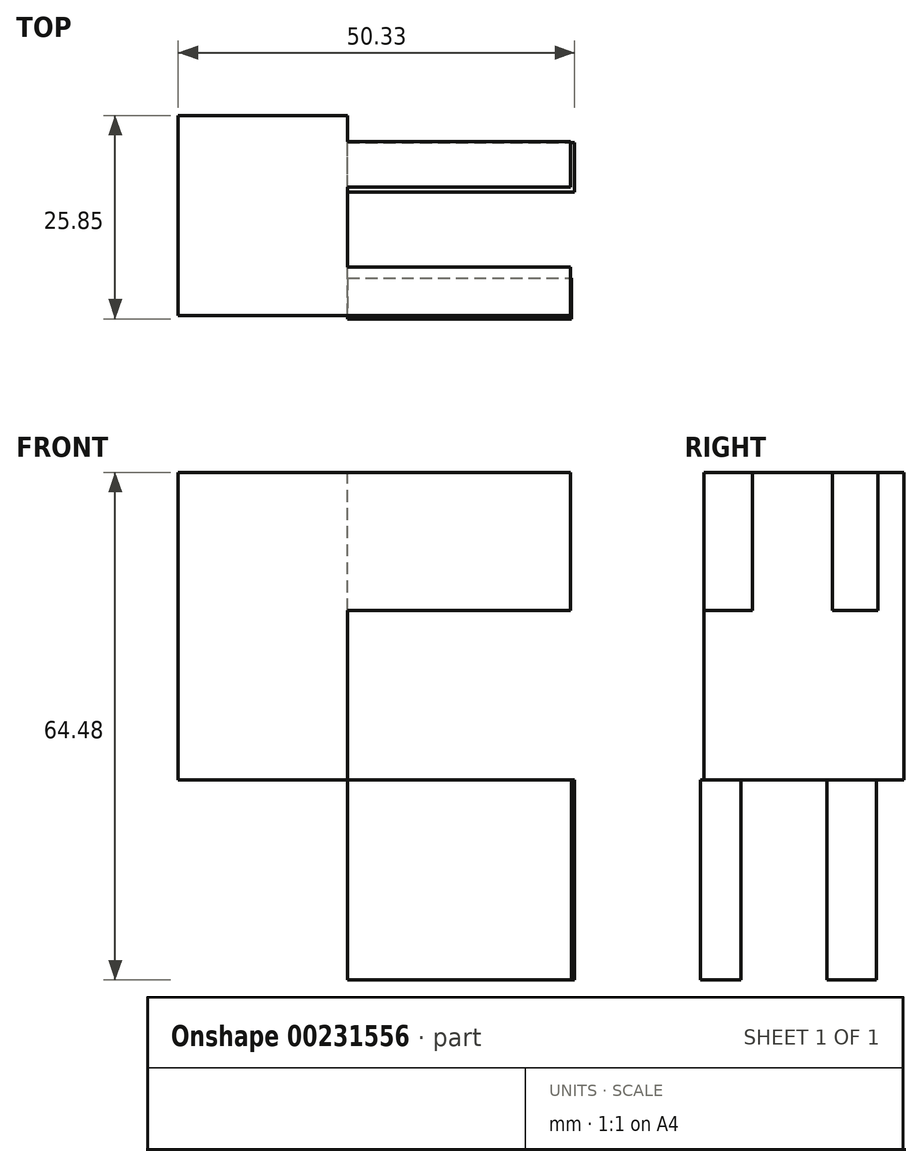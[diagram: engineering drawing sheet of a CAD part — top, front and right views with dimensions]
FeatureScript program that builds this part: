
annotation { "Feature Type Name" : "Feature", "Feature Type Description" : "" }
export const myFeature = defineFeature(function(context is Context, id is Id, definition is map)
    precondition{}
    {
        {
            var Q0;
            Q0=qCreatedBy(makeId("Front.planeOp"),FACE);
            var sketch = newSketch(context, id + "F0", { "sketchPlane" : qUnion([Q0])});
            skLineSegment(sketch, "E0.bottom", {"start": v(-22.74, 6) * mm, "end": v(21.5, 6) * mm});
            skLineSegment(sketch, "E0.top", {"start": v(-22.74, -18.81) * mm, "end": v(21.5, -18.81) * mm});
            skLineSegment(sketch, "E0.left", {"start": v(-22.74, 6) * mm, "end": v(-22.74, -18.81) * mm});
            skLineSegment(sketch, "E0.right", {"start": v(21.5, 6) * mm, "end": v(21.5, -18.81) * mm});
            skSolve(sketch);
        }
        {
            var Q0;
            Q0=makeQuery(id+"F0.imprint","IMPRINT",FACE,{"disambiguationData":[TD([[makeQuery(id+"F0.imprint","IMPRINT",EDGE,{"derivedFrom":sQuery(id+"F0.wireOp",EDGE,"E0.bottom")}),-1.0]])]});
            var sketch = newSketch(context, id + "F1", { "sketchPlane" : qUnion([Q0])});
            skLineSegment(sketch, "E1.bottom", {"start": v(43.2, 14.06) * mm, "end": v(21.7, 14.06) * mm});
            skLineSegment(sketch, "E1.top", {"start": v(43.2, -25.02) * mm, "end": v(21.7, -25.02) * mm});
            skLineSegment(sketch, "E1.left", {"start": v(43.2, 14.06) * mm, "end": v(43.2, -25.02) * mm});
            skLineSegment(sketch, "E1.right", {"start": v(21.7, 14.06) * mm, "end": v(21.7, -25.02) * mm});
            skSolve(sketch);
        }
        {
            var Q0;
            Q0 = qSketchRegion(id + "F1", true);
            extrude(context, id + "F2", {"entities" : qUnion([Q0]), "depth" : 25.4 * mm});
        }
        {
            var Q0;
            Q0=makeQuery(id+"F2.opExtrude","SWEPT_FACE",FACE,{"disambiguationData":[OSD([sQuery(id+"F1.wireOp",EDGE,"E1.bottom")])]});
            var sketch = newSketch(context, id + "F3", { "sketchPlane" : qUnion([Q0])});
            skLineSegment(sketch, "E2.bottom", {"start": v(43.2, -3.3) * mm, "end": v(71.53, -3.3) * mm});
            skLineSegment(sketch, "E2.top", {"start": v(43.2, -9.1) * mm, "end": v(71.53, -9.1) * mm});
            skLineSegment(sketch, "E2.left", {"start": v(43.2, -3.3) * mm, "end": v(43.2, -9.1) * mm});
            skLineSegment(sketch, "E2.right", {"start": v(71.53, -3.3) * mm, "end": v(71.53, -9.1) * mm});
            skLineSegment(sketch, "E3.bottom", {"start": v(43.2, -19.23) * mm, "end": v(71.53, -19.23) * mm});
            skLineSegment(sketch, "E3.top", {"start": v(43.2, -25.4) * mm, "end": v(71.53, -25.4) * mm});
            skLineSegment(sketch, "E3.left", {"start": v(43.2, -19.23) * mm, "end": v(43.2, -25.4) * mm});
            skLineSegment(sketch, "E3.right", {"start": v(71.53, -19.23) * mm, "end": v(71.53, -25.4) * mm});
            skSolve(sketch);
        }
        {
            var Q0;
            Q0=makeQuery(id+"F3.imprint","IMPRINT",FACE,{"disambiguationData":[TD([[makeQuery(id+"F3.imprint","IMPRINT",EDGE,{"derivedFrom":sQuery(id+"F3.wireOp",EDGE,"E3.bottom")}),-1.0]])]});
            var Q1;
            Q1=makeQuery(id+"F3.imprint","IMPRINT",FACE,{"disambiguationData":[TD([[makeQuery(id+"F3.imprint","IMPRINT",EDGE,{"derivedFrom":sQuery(id+"F3.wireOp",EDGE,"E2.bottom")}),-1.0]])]});
            extrude(context, id + "F4", {"entities" : qUnion([Q0, Q1]), "operationType" : NewBodyOperationType.ADD, "oppositeDirection" : true, "depth" : 17.53 * mm});
        }
        {
            var Q0;
            Q0=makeQuery(id+"F2.opExtrude","SWEPT_FACE",FACE,{"disambiguationData":[OSD([sQuery(id+"F1.wireOp",EDGE,"E1.top")])]});
            var sketch = newSketch(context, id + "F5", { "sketchPlane" : qUnion([Q0])});
            skLineSegment(sketch, "E4.left", {"start": v(43.2, 22.95) * mm, "end": v(43.2, 20.67) * mm});
            skLineSegment(sketch, "E4.right", {"start": v(54.17, 22.95) * mm, "end": v(54.17, 20.67) * mm});
            skLineSegment(sketch, "E5.bottom", {"start": v(43.2, 20.67) * mm, "end": v(71.65, 20.67) * mm});
            skLineSegment(sketch, "E5.top", {"start": v(43.2, 25.85) * mm, "end": v(71.65, 25.85) * mm});
            skLineSegment(sketch, "E5.left", {"start": v(43.2, 20.67) * mm, "end": v(43.2, 25.85) * mm});
            skLineSegment(sketch, "E5.right", {"start": v(71.65, 20.67) * mm, "end": v(71.65, 25.85) * mm});
            skLineSegment(sketch, "E6.bottom", {"start": v(43.2, 9.75) * mm, "end": v(72.04, 9.75) * mm});
            skLineSegment(sketch, "E6.top", {"start": v(43.2, 3.47) * mm, "end": v(72.04, 3.47) * mm});
            skLineSegment(sketch, "E6.left", {"start": v(43.2, 9.75) * mm, "end": v(43.2, 3.47) * mm});
            skLineSegment(sketch, "E6.right", {"start": v(72.04, 9.75) * mm, "end": v(72.04, 3.47) * mm});
            skSolve(sketch);
        }
        {
            var Q0;
            Q0 = qSketchRegion(id + "F5", true);
            extrude(context, id + "F6", {"entities" : qUnion([Q0]), "depth" : 25.4 * mm});
        }
    });
